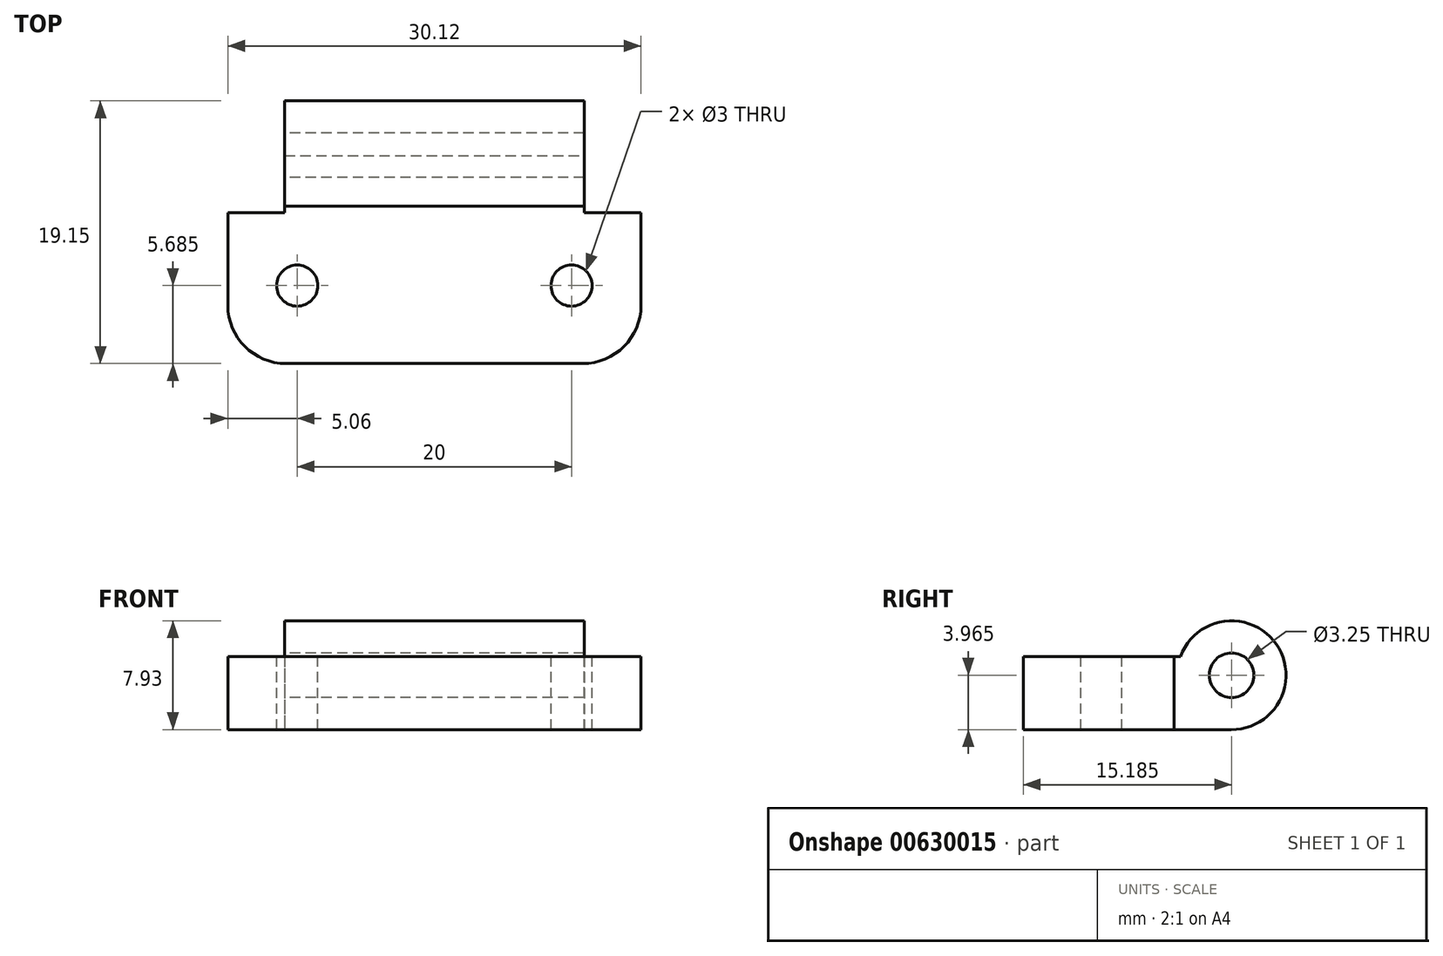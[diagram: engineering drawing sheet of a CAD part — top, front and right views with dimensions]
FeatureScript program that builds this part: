
annotation { "Feature Type Name" : "Feature", "Feature Type Description" : "" }
export const myFeature = defineFeature(function(context is Context, id is Id, definition is map)
    precondition{}
    {
        {
            var Q0;
            Q0=qCreatedBy(makeId("Top.planeOp"),FACE);
            var sketch = newSketch(context, id + "F0", { "sketchPlane" : qUnion([Q0])});
            skLineSegment(sketch, "E0", {"start": v(0, 0) * mm, "end": v(-10.8, 0) * mm});
            skLineSegment(sketch, "E1", {"start": v(-15.06, 4.25) * mm, "end": v(-15.06, 11) * mm});
            skLineSegment(sketch, "E2", {"start": v(-15.06, 11) * mm, "end": v(-10.91, 11) * mm});
            skLineSegment(sketch, "E3", {"start": v(0, 0) * mm, "end": v(0, 11) * mm, "construction": true});
            skLineSegment(sketch, "E4", {"start": v(0, 11) * mm, "end": v(-10.91, 11) * mm, "construction": true});
            skPoint(sketch, "E5.visualSharp", {"position": v(-15.06, 0) * mm});
            skArc(sketch, "E5.filletArc", {"start": v(-15.06, 4.25) * mm, "mid": v(-13.82, 1.24) * mm, "end": v(-10.8, 0) * mm});
            skLineSegment(sketch, "E6.MirrorCS", {"start": v(0, 11) * mm, "end": v(10.91, 11) * mm, "construction": true});
            skLineSegment(sketch, "E7.MirrorCS", {"start": v(15.06, 11) * mm, "end": v(10.91, 11) * mm});
            skLineSegment(sketch, "E8.MirrorCS", {"start": v(15.06, 4.25) * mm, "end": v(15.06, 11) * mm});
            skArc(sketch, "E9.MirrorCS", {"start": v(15.06, 4.25) * mm, "mid": v(13.82, 1.24) * mm, "end": v(10.8, 0) * mm});
            skLineSegment(sketch, "E10.MirrorCS", {"start": v(0, 0) * mm, "end": v(10.8, 0) * mm});
            skLineSegment(sketch, "E11", {"start": v(-10.91, 11) * mm, "end": v(-10.91, 15.15) * mm});
            skLineSegment(sketch, "E12", {"start": v(-10.9, 15.15) * mm, "end": v(10.9, 15.15) * mm});
            skLineSegment(sketch, "E13", {"start": v(10.91, 15.15) * mm, "end": v(10.91, 11) * mm});
            skSolve(sketch);
        }
        {
            var Q0;
            Q0 = qSketchRegion(id + "F0", true);
            extrude(context, id + "F1", {"entities" : qUnion([Q0]), "depth" : 5.32 * mm, "offsetDistance" : 25 * mm});
        }
        {
            var Q0;
            Q0=makeQuery(id+"F1.opExtrude","SWEPT_FACE",FACE,{"disambiguationData":[OSD([sQuery(id+"F0.wireOp",EDGE,"E11")])]});
            var sketch = newSketch(context, id + "F2", { "sketchPlane" : qUnion([Q0])});
            skCircle(sketch, "E14", {"center": v(-15.18, 3.97) * mm, "radius": 3.96 * mm});
            skLineSegment(sketch, "E15", {"start": v(-15.15, 0) * mm, "end": v(-25.38, 0) * mm, "construction": true});
            skCircle(sketch, "E16", {"center": v(-15.18, 3.97) * mm, "radius": 1.63 * mm});
            skLineSegment(sketch, "E17", {"start": v(-19.15, 0) * mm, "end": v(-19.15, 10.07) * mm, "construction": true});
            skLineSegment(sketch, "E18", {"start": v(-15.18, 3.97) * mm, "end": v(-15.18, -1.56) * mm, "construction": true});
            skSolve(sketch);
        }
        {
            var Q0;
            {var subQ0=sQuery(id+"F2.wireOp",EDGE,"E14");var subQ1=sQuery(id+"F0.wireOp",EDGE,"E11");var subQ4=makeQuery(id+"F1.opExtrude","CAP_EDGE",EDGE,{"disambiguationData":[OSD([subQ1])],"isStart":false});var subQ5=makeQuery(id+"F2.imprint","INTERSECT",VERTEX,{"derivedFrom":[subQ4,subQ0]});Q0=makeQuery(id+"F2.imprint","IMPRINT",FACE,{"disambiguationData":[TD([[makeQuery(id+"F2.imprint","IMPRINT",EDGE,{"disambiguationData":[TD([[subQ5,-1.0]])],"derivedFrom":subQ4}),-1.0]])]});}
            var Q1;
            {var subQ0=sQuery(id+"F2.wireOp",EDGE,"E16");var subQ1=sQuery(id+"F0.wireOp",EDGE,"E11");var subQ4=makeQuery(id+"F1.opExtrude","CAP_EDGE",EDGE,{"disambiguationData":[OSD([subQ1])],"isStart":false});var subQ5=makeQuery(id+"F2.imprint","INTERSECT",VERTEX,{"derivedFrom":[subQ4,subQ0]});Q1=makeQuery(id+"F2.imprint","IMPRINT",FACE,{"disambiguationData":[TD([[makeQuery(id+"F2.imprint","IMPRINT",EDGE,{"disambiguationData":[TD([[subQ5,-1.0]])],"derivedFrom":subQ0}),1.0]])]});}
            var Q2;
            Q2=makeQuery(id+"F1.opExtrude","SWEPT_FACE",FACE,{"disambiguationData":[OSD([sQuery(id+"F0.wireOp",EDGE,"E13")])]});
            extrude(context, id + "F3", {"entities" : qUnion([Q0, Q1]), "operationType" : NewBodyOperationType.ADD, "endBound" : BoundingType.UP_TO_SURFACE, "oppositeDirection" : true, "depth" : 25 * mm, "endBoundEntityFace" : qUnion([Q2]), "offsetDistance" : 25 * mm});
        }
        {
            var Q0;
            {var subQ0=sQuery(id+"F2.wireOp",EDGE,"E16");var subQ1=sQuery(id+"F0.wireOp",EDGE,"E11");var subQ4=makeQuery(id+"F1.opExtrude","CAP_EDGE",EDGE,{"disambiguationData":[OSD([subQ1])],"isStart":false});var subQ5=makeQuery(id+"F2.imprint","INTERSECT",VERTEX,{"derivedFrom":[subQ4,subQ0]});Q0=makeQuery(id+"F2.imprint","IMPRINT",FACE,{"disambiguationData":[TD([[makeQuery(id+"F2.imprint","IMPRINT",EDGE,{"disambiguationData":[TD([[subQ5,-1.0]])],"derivedFrom":subQ0}),1.0]])]});}
            var Q1;
            {var subQ0=sQuery(id+"F2.wireOp",EDGE,"E16");var subQ1=sQuery(id+"F0.wireOp",EDGE,"E11");var subQ4=makeQuery(id+"F1.opExtrude","CAP_EDGE",EDGE,{"disambiguationData":[OSD([subQ1])],"isStart":false});var subQ5=makeQuery(id+"F2.imprint","INTERSECT",VERTEX,{"derivedFrom":[subQ4,subQ0]});Q1=makeQuery(id+"F2.imprint","IMPRINT",FACE,{"disambiguationData":[TD([[makeQuery(id+"F2.imprint","IMPRINT",EDGE,{"disambiguationData":[TD([[subQ5,1.0]])],"derivedFrom":subQ0}),1.0]])]});}
            extrude(context, id + "F4", {"entities" : qUnion([Q0, Q1]), "operationType" : NewBodyOperationType.REMOVE, "endBound" : BoundingType.THROUGH_ALL, "oppositeDirection" : true, "depth" : 25 * mm, "offsetDistance" : 25 * mm});
        }
        {
            var Q0;
            Q0=makeQuery(id+"F1.opExtrude","CAP_FACE",FACE,{"disambiguationData":[OSD([sQuery(id+"F0.wireOp",EDGE,"E0"),sQuery(id+"F0.wireOp",EDGE,"E1"),sQuery(id+"F0.wireOp",EDGE,"E2"),sQuery(id+"F0.wireOp",EDGE,"E5.filletArc"),sQuery(id+"F0.wireOp",EDGE,"E7.MirrorCS"),sQuery(id+"F0.wireOp",EDGE,"E8.MirrorCS"),sQuery(id+"F0.wireOp",EDGE,"E9.MirrorCS"),sQuery(id+"F0.wireOp",EDGE,"E10.MirrorCS"),sQuery(id+"F0.wireOp",EDGE,"E11"),sQuery(id+"F0.wireOp",EDGE,"E12"),sQuery(id+"F0.wireOp",EDGE,"E13")])],"isStart":false});
            var sketch = newSketch(context, id + "F5", { "sketchPlane" : qUnion([Q0])});
            skLineSegment(sketch, "E19", {"start": v(-10, 5.68) * mm, "end": v(10, 5.69) * mm, "construction": true});
            skCircle(sketch, "E20", {"center": v(-10, 5.68) * mm, "radius": 1.5 * mm});
            skCircle(sketch, "E21", {"center": v(10, 5.69) * mm, "radius": 1.5 * mm});
            skLineSegment(sketch, "E22", {"start": v(0, 0) * mm, "end": v(0, 9.66) * mm, "construction": true});
            skPoint(sketch, "E22.endSnap0", {"position": v(0, 11.46) * mm});
            skSolve(sketch);
        }
        {
            var Q0;
            Q0=makeQuery(id+"F5.imprint","IMPRINT",FACE,{"disambiguationData":[TD([[makeQuery(id+"F5.imprint","IMPRINT",EDGE,{"derivedFrom":sQuery(id+"F5.wireOp",EDGE,"E20")}),1.0]])]});
            var Q1;
            Q1=makeQuery(id+"F5.imprint","IMPRINT",FACE,{"disambiguationData":[TD([[makeQuery(id+"F5.imprint","IMPRINT",EDGE,{"derivedFrom":sQuery(id+"F5.wireOp",EDGE,"E21")}),1.0]])]});
            extrude(context, id + "F6", {"entities" : qUnion([Q0, Q1]), "operationType" : NewBodyOperationType.REMOVE, "endBound" : BoundingType.THROUGH_ALL, "oppositeDirection" : true, "depth" : 25 * mm, "offsetDistance" : 25 * mm});
        }
    });
